# Revit family: IS_Tesi_Multiproduct_BIM_IT_T3536;T3537
name_source: partatom
category: Plumbing Fixtures
units: mm (PartAtom-declared; Revit-internal decimal feet)

## family parameters
Cut with Voids When Loaded = No
Host = Face
OmniClass Number = 23.45.05.21.11.11
OmniClass Title = Water Operated Water Closets
Part Type = Normal
Room Calculation Point = No
Round Connector Dimension = Use Diameter
Shared = Yes

## types (2) — shared parameters
Accessori = www.idealstandard.it
AltezzaNominale = 400 mm
Assembly Code = C1030200
Autore = Ideal Standard
Brand = Ideal Standard
Caratteristiche = Vaso a terra filo parete AquaBlade® completo di sedile slim a chiusura rallentata e sgancio rapido.
Connessione = Installazione
Description = Vaso a terra filo parete AquaBlade® completo di sedile slim a chiusura rallentata e sgancio rapido.
DescrizioneClassifcazioneUni2015 = WC pans
Dimensione = 400 x 551 x 360 mm
DurataGaranzia = 99
DurataGaranziaLegale = 99
DurataGaranziaProdotti = 99
Forma = scolpito
Garanzia = Garanzia Idealstandard
IfcEsportaCome = IfcSanitaryTerminalType
InformaziniGaranzia = www.idealstandard.it/garanzia.html
InformazioniDiProdotto = www.idealstandard.it/prodotti/html
InformazioniGaranzia = www.idealstandard.it/garanzia.html
InstruzioniInstallazione = www.idealstandard.it/prodotti/html
LarghezzaNominale = 360 mm
LunghezzaNominale = 550 mm
ModelloDiRiferimento = TESI VASO MULTI BTW AB BEU SED SLIM SOFT
NBSDescription = WC pans
NBSReference = 45-30-70/384
Nome = WcPans_TESI_T353601_IdealStandard
NomeOggettoBim = ISI_IdealStandard_WcPans_TESI_T353601
PesoNetto = 28 Kg
Produttore = www.idealstandard.it
ProfonditàNominale = 550 mm
Revisione = 1
RiferimentoClassificazioneUni2015 = Pr_40_20_93_94
Spazio = interno
Telefono = 800 652 290
TipoEspotazioneIfc = WCPANS
URL = www.idealstandard.it
UnitàDurata = anni
UnitàDurataGaranzia = anni
UnitàVolume = Litri
Versione = 1
VersioneClassificazioneUni2015 = v1.20
zero-valued in all types: CWFU, Cost, CostoDiSostituzione, Default Elevation, HWFU, SpilloverLivello, WFU

## per-type parameters (varying)
| type | CodiceABarre | Finitura | Material | Model | NumeroDiModello |
| T3536V3 - Tesi WC back to wall bowl with slow close seat and cover - silk black | 8014140485537 | Nero Seta | IS_RenderMaterial_VitreousChina_Silk_Black | T3536V3 | T3536V3 |
| T353601 - Tesi WC back to wall bowl with slow close seat and cover - White | 8014140430407 | Bianco | IS_RenderMaterial_VitreousChina_White | T353601 | T353601 |

## geometry (parser evidence)
native form markers: Sweep x1
no freeform markers — native parametric forms only
